# Revit family: Шаровой кран с удлиненной Т-образной полимерной рукояткой и термометром(цвет рукоятки - синий) 2201
name_source: partatom
category: Rohrzubehör
revit_build: Autodesk Revit 2018 (Build: 20190510_1515(x64)
units: mm (PartAtom-declared; Revit-internal decimal feet)

## family parameters
Arbeitsebenenbasiert = Nein
Beim Laden mit Abzugskörper schneiden = Nein
Bemaßung runder Anschluss = Durchmesser verwenden
Gemeinsam genutzt = Nein
Immer vertikal = Ja
OmniClass-Nummer = 23.65.55.14
OmniClass-Titel = Valves for Liquid Services
Teiletyp = Unterbricht

## types (2) — shared parameters
Hersteller = HERZ Armaturen Ges.m.b.H
SCRNCODE = 05;10;02
SCRNSEQ = ARM;ARM_TYP="ABVS";2
URL = www.herz-armaturen.ru
W01 = 135.00°
Внутренняя резьба = в соответствии с ISO 228-1
Корпус = штампованная латунь в соответствии с  EN 12165, никелированный, CW617N
Макс. рабочая температура = 150 °C
Макс. рабочая температура (вода - не пар) = 110 °C
Макс. рабочее давление = 2500000.0 Pa
Макс. рабочее давление (соединения) = 1600000.0 Pa
Мин. рабочая температура = -30 °C
Мин. рабочая температура (вода) = 1 °C
Область применения = Шаровой кран используется в качестве запорной арматуры в системе. Область применения - системы отопления и холодоснабжения. Рабочие параметры (температура и давление) должны соблюдаться.
Применение = Шаровые краны используются для перекрытия трубопроводов систем отопления и холодоснабжения. Шаровые краны не должны использоваться в качестве регулирующей арматуры, поэтому они должны быть полностью открыты или закрыты.
Рукоятка = удлиненная Т-образная рукоятка с термометром, цвет - синий, из пластика PA66 GF30
Среда = Качество теплоносителя в соответствии с ÖNORM H5195 и/или предписаниями VDI 2035.
Разрешается использование смеси этилен или пропиленгликоля в соотношении 25-50% с водой.
Уплотнение шара = PTFE
Уплотнение шпинделя = PTFE
Шар = штампованная латунь в соответствии с EN 12165, хромированный полнопроходной шар, CW617N
Шпиндель = латунь в соответствии с EN 12164, CW614N

## per-type parameters (varying)
| type | Dämmung |
| С теплоизолирующим кожухом | Ja |
| Без теплоизолирующего кожуха | Nein |
